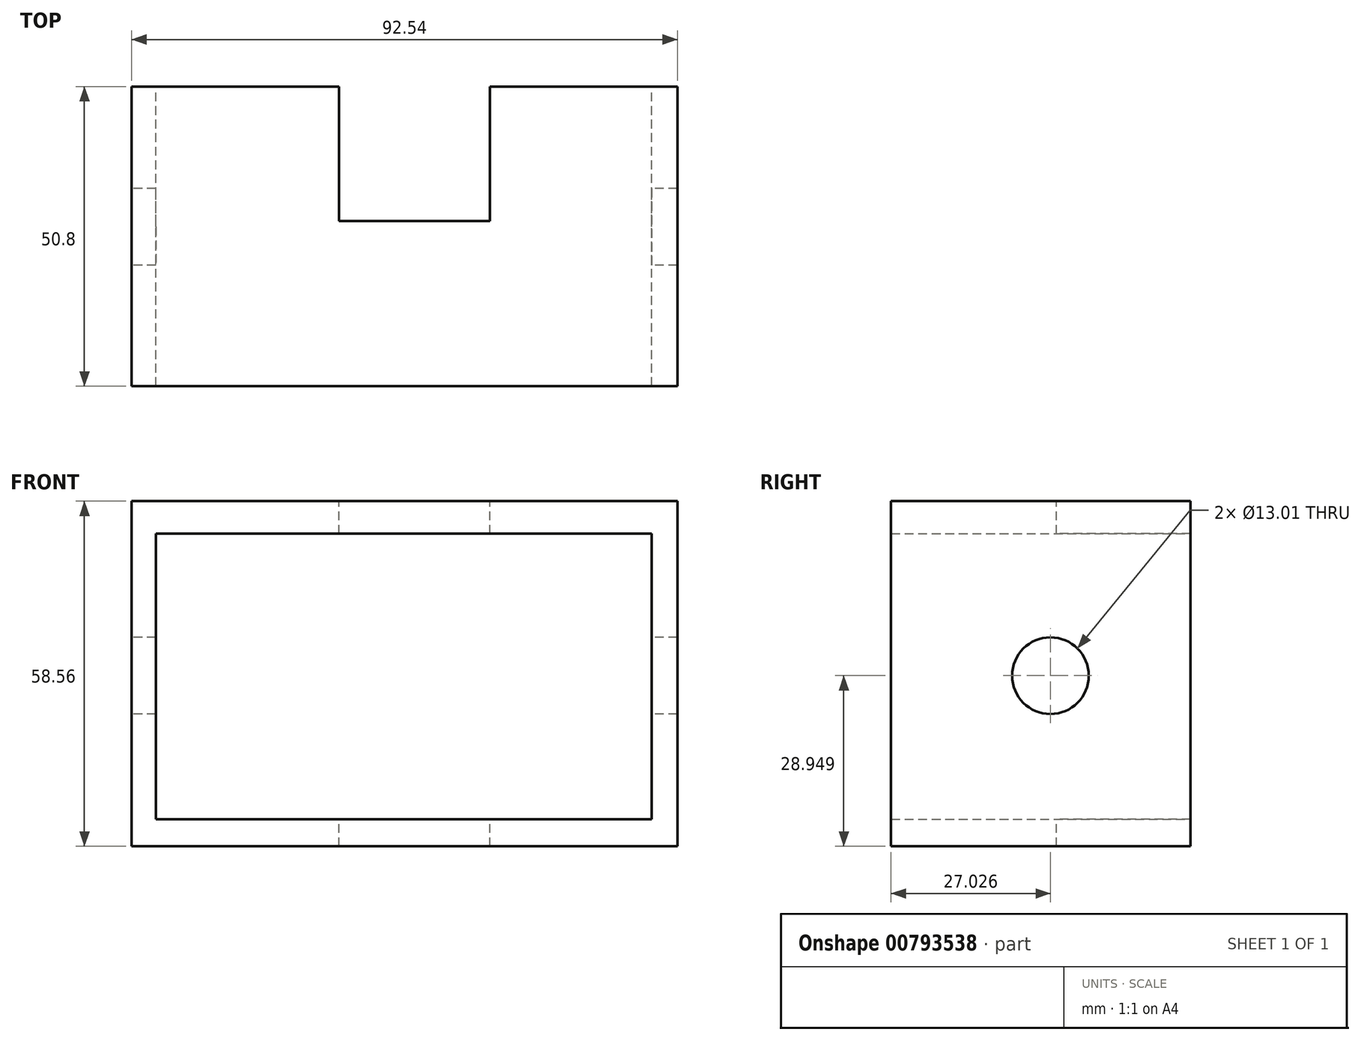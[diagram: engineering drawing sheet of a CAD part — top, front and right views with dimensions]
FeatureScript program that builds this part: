
annotation { "Feature Type Name" : "Feature", "Feature Type Description" : "" }
export const myFeature = defineFeature(function(context is Context, id is Id, definition is map)
    precondition{}
    {
        {
            var Q0;
            Q0=qCreatedBy(makeId("Front.planeOp"),FACE);
            var sketch = newSketch(context, id + "F0", { "sketchPlane" : qUnion([Q0])});
            skLineSegment(sketch, "E0.bottom", {"start": v(-44.7, 22.05) * mm, "end": v(47.84, 22.05) * mm});
            skLineSegment(sketch, "E0.top", {"start": v(-44.7, -36.51) * mm, "end": v(47.84, -36.51) * mm});
            skLineSegment(sketch, "E0.left", {"start": v(-44.7, 22.05) * mm, "end": v(-44.7, -36.51) * mm});
            skLineSegment(sketch, "E0.right", {"start": v(47.84, 22.05) * mm, "end": v(47.84, -36.51) * mm});
            skSolve(sketch);
        }
        {
            var Q0;
            Q0 = qSketchRegion(id + "F0", true);
            extrude(context, id + "F1", {"entities" : qUnion([Q0]), "depth" : 50.8 * mm, "offsetDistance" : 25.4 * mm});
        }
        {
            var Q0;
            Q0=qCreatedBy(makeId("Front.planeOp"),FACE);
            var sketch = newSketch(context, id + "F2", { "sketchPlane" : qUnion([Q0])});
            skLineSegment(sketch, "E1.bottom", {"start": v(-40.6, 16.5) * mm, "end": v(43.5, 16.5) * mm});
            skLineSegment(sketch, "E1.top", {"start": v(-40.6, -31.93) * mm, "end": v(43.5, -31.93) * mm});
            skLineSegment(sketch, "E1.left", {"start": v(-40.6, 16.5) * mm, "end": v(-40.6, -31.93) * mm});
            skLineSegment(sketch, "E1.right", {"start": v(43.5, 16.5) * mm, "end": v(43.5, -31.93) * mm});
            skSolve(sketch);
        }
        {
            var Q0;
            Q0=makeQuery(id+"F2.imprint","IMPRINT",FACE,{"disambiguationData":[TD([[makeQuery(id+"F2.imprint","IMPRINT",EDGE,{"derivedFrom":sQuery(id+"F2.wireOp",EDGE,"E1.bottom")}),-1.0]])]});
            extrude(context, id + "F3", {"entities" : qUnion([Q0]), "operationType" : NewBodyOperationType.REMOVE, "depth" : 51.3 * mm, "offsetDistance" : 25.4 * mm});
        }
        {
            var Q0;
            Q0=makeQuery(id+"F1.opExtrude","SWEPT_FACE",FACE,{"disambiguationData":[OSD([sQuery(id+"F0.wireOp",EDGE,"E0.bottom")])]});
            var sketch = newSketch(context, id + "F4", { "sketchPlane" : qUnion([Q0])});
            skLineSegment(sketch, "E2.bottom", {"start": v(-9.52, 0) * mm, "end": v(16.03, 0) * mm});
            skLineSegment(sketch, "E2.top", {"start": v(-9.52, -22.77) * mm, "end": v(16.03, -22.77) * mm});
            skLineSegment(sketch, "E2.left", {"start": v(-9.52, 0) * mm, "end": v(-9.52, -22.77) * mm});
            skLineSegment(sketch, "E2.right", {"start": v(16.03, 0) * mm, "end": v(16.03, -22.77) * mm});
            skSolve(sketch);
        }
        {
            var Q0;
            Q0=makeQuery(id+"F4.imprint","IMPRINT",FACE,{"disambiguationData":[TD([[makeQuery(id+"F4.imprint","IMPRINT",EDGE,{"derivedFrom":sQuery(id+"F4.wireOp",EDGE,"E2.bottom")}),-1.0]])]});
            extrude(context, id + "F5", {"entities" : qUnion([Q0]), "operationType" : NewBodyOperationType.REMOVE, "oppositeDirection" : true, "depth" : 58.93 * mm, "offsetDistance" : 25.4 * mm});
        }
        {
            var Q0;
            Q0=makeQuery(id+"F1.opExtrude","SWEPT_FACE",FACE,{"disambiguationData":[OSD([sQuery(id+"F0.wireOp",EDGE,"E0.left")])]});
            var sketch = newSketch(context, id + "F6", { "sketchPlane" : qUnion([Q0])});
            skCircle(sketch, "E3", {"center": v(23.77, -7.56) * mm, "radius": 6.5 * mm});
            skSolve(sketch);
        }
        {
            var Q0;
            Q0=makeQuery(id+"F6.imprint","IMPRINT",FACE,{"disambiguationData":[TD([[makeQuery(id+"F6.imprint","IMPRINT",EDGE,{"derivedFrom":sQuery(id+"F6.wireOp",EDGE,"E3")}),1.0]])]});
            extrude(context, id + "F7", {"entities" : qUnion([Q0]), "operationType" : NewBodyOperationType.REMOVE, "oppositeDirection" : true, "depth" : 110.24 * mm, "offsetDistance" : 25.4 * mm});
        }
    });
